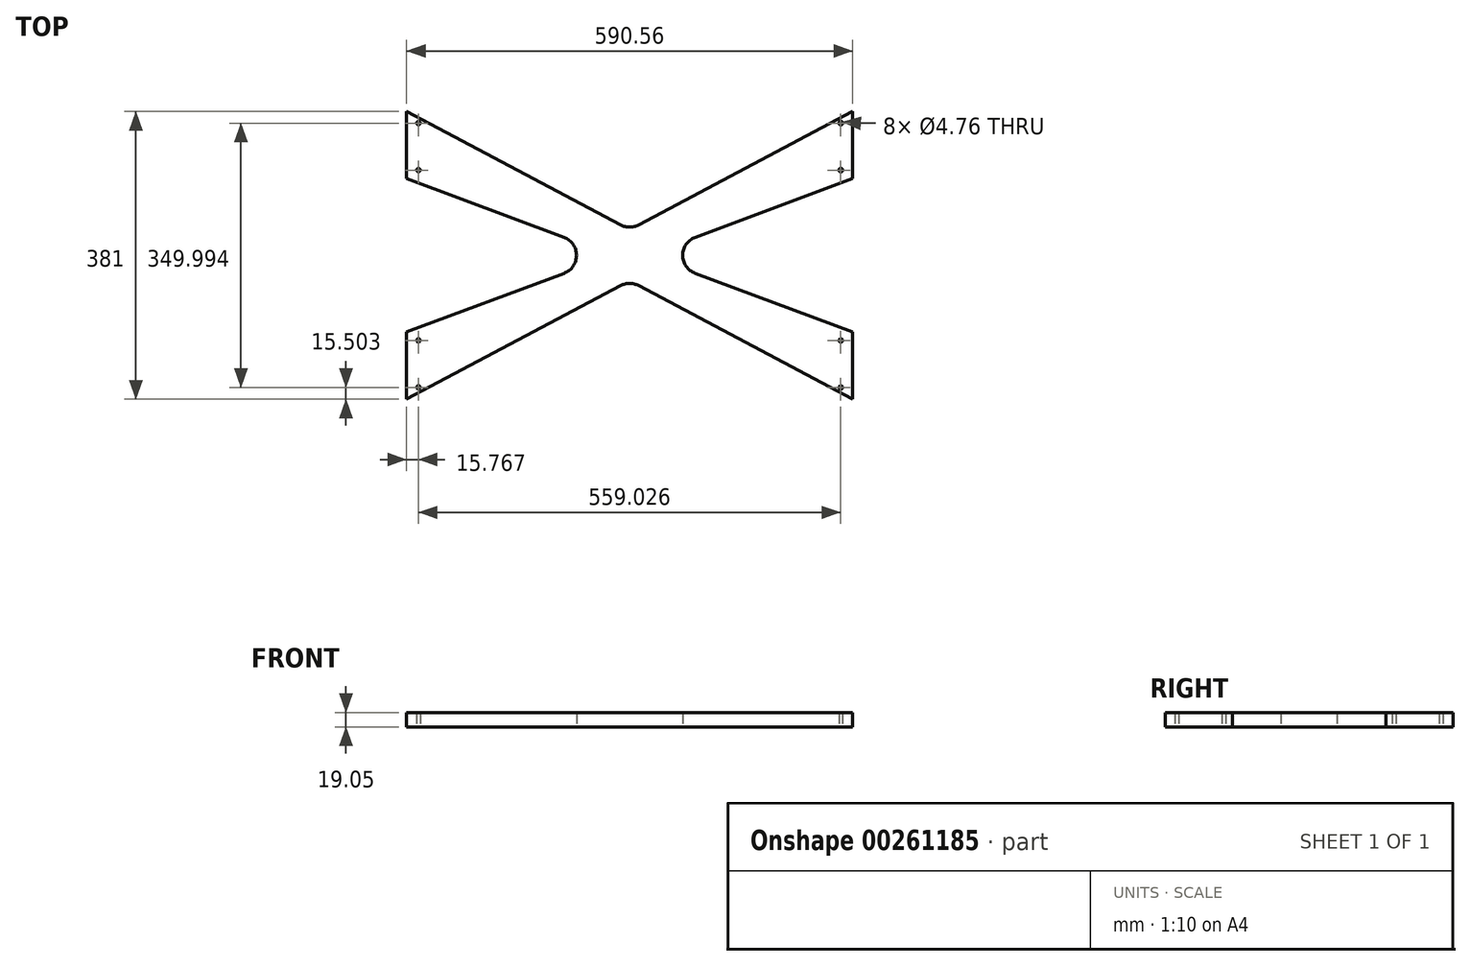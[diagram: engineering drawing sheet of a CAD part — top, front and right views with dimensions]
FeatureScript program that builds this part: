
annotation { "Feature Type Name" : "Feature", "Feature Type Description" : "" }
export const myFeature = defineFeature(function(context is Context, id is Id, definition is map)
    precondition{}
    {
        {
            var Q0;
            Q0=qCreatedBy(makeId("Top.planeOp"),FACE);
            var sketch = newSketch(context, id + "F0", { "sketchPlane" : qUnion([Q0])});
            skLineSegment(sketch, "E0.bottom", {"start": v(-295.28, 190.5) * mm, "end": v(295.27, 190.5) * mm, "construction": true});
            skLineSegment(sketch, "E0.top", {"start": v(-295.28, -190.5) * mm, "end": v(295.27, -190.5) * mm, "construction": true});
            skLineSegment(sketch, "E0.left", {"start": v(-295.28, 190.5) * mm, "end": v(-295.28, -190.5) * mm, "construction": true});
            skLineSegment(sketch, "E0.right", {"start": v(295.27, 190.5) * mm, "end": v(295.27, -190.5) * mm, "construction": true});
            skPoint(sketch, "E0.middle", {"position": v(0, 0) * mm});
            skLineSegment(sketch, "E1", {"start": v(-295.28, 190.5) * mm, "end": v(-295.28, 101.6) * mm});
            skLineSegment(sketch, "E2", {"start": v(-295.28, 0) * mm, "end": v(295.27, 0) * mm, "construction": true});
            skLineSegment(sketch, "E3", {"start": v(0, 190.5) * mm, "end": v(0, -190.5) * mm, "construction": true});
            skLineSegment(sketch, "E4", {"start": v(-295.28, 101.6) * mm, "end": v(-86.78, 23.8) * mm});
            skLineSegment(sketch, "E5.MirrorCS", {"start": v(-295.28, -101.6) * mm, "end": v(-86.78, -23.8) * mm});
            skLineSegment(sketch, "E6.MirrorCS", {"start": v(-295.28, -190.5) * mm, "end": v(-295.28, -101.6) * mm});
            skLineSegment(sketch, "E7.MirrorCS", {"start": v(295.28, 190.5) * mm, "end": v(295.28, 101.6) * mm});
            skLineSegment(sketch, "E8.MirrorCS", {"start": v(295.28, 101.6) * mm, "end": v(86.78, 23.8) * mm});
            skLineSegment(sketch, "E9.MirrorCS", {"start": v(295.28, -101.6) * mm, "end": v(86.78, -23.8) * mm});
            skLineSegment(sketch, "E10.MirrorCS", {"start": v(295.28, -190.5) * mm, "end": v(295.28, -101.6) * mm});
            skLineSegment(sketch, "E11", {"start": v(-295.28, 190.5) * mm, "end": v(-11.9, 40.21) * mm});
            skLineSegment(sketch, "E12.MirrorCS", {"start": v(295.28, 190.5) * mm, "end": v(11.9, 40.21) * mm});
            skLineSegment(sketch, "E13.MirrorCS", {"start": v(295.28, -190.5) * mm, "end": v(11.9, -40.21) * mm});
            skLineSegment(sketch, "E14.MirrorCS", {"start": v(-295.28, -190.5) * mm, "end": v(-11.9, -40.21) * mm});
            skPoint(sketch, "E15.visualSharp", {"position": v(0, 33.9) * mm});
            skArc(sketch, "E15.filletArc", {"start": v(-11.9, 40.21) * mm, "mid": v(0, 37.25) * mm, "end": v(11.9, 40.21) * mm});
            skPoint(sketch, "E16.visualSharp", {"position": v(23.01, 0) * mm});
            skArc(sketch, "E16.filletArc", {"start": v(86.78, 23.8) * mm, "mid": v(70.26, 0) * mm, "end": v(86.78, -23.8) * mm});
            skPoint(sketch, "E17.visualSharp", {"position": v(-23.01, 0) * mm});
            skArc(sketch, "E17.filletArc", {"start": v(-86.78, -23.8) * mm, "mid": v(-70.26, 0) * mm, "end": v(-86.78, 23.8) * mm});
            skPoint(sketch, "E18.visualSharp", {"position": v(0, -33.9) * mm});
            skArc(sketch, "E18.filletArc", {"start": v(11.9, -40.21) * mm, "mid": v(0, -37.25) * mm, "end": v(-11.9, -40.21) * mm});
            skCircle(sketch, "E19", {"center": v(-279.51, 175) * mm, "radius": 2.38 * mm});
            skCircle(sketch, "E20", {"center": v(-279.51, 112.8) * mm, "radius": 2.38 * mm});
            skCircle(sketch, "E21.MirrorC", {"center": v(-279.51, -175) * mm, "radius": 2.38 * mm});
            skCircle(sketch, "E22.MirrorC", {"center": v(-279.51, -112.8) * mm, "radius": 2.38 * mm});
            skCircle(sketch, "E23.MirrorC", {"center": v(279.51, 175) * mm, "radius": 2.38 * mm});
            skCircle(sketch, "E24.MirrorC", {"center": v(279.51, 112.8) * mm, "radius": 2.38 * mm});
            skCircle(sketch, "E25.MirrorC", {"center": v(279.51, -112.8) * mm, "radius": 2.38 * mm});
            skCircle(sketch, "E26.MirrorC", {"center": v(279.51, -175) * mm, "radius": 2.38 * mm});
            skSolve(sketch);
        }
        {
            var Q0;
            Q0 = qSketchRegion(id + "F0", true);
            extrude(context, id + "F1", {"entities" : qUnion([Q0]), "depth" : 19.05 * mm});
        }
    });
